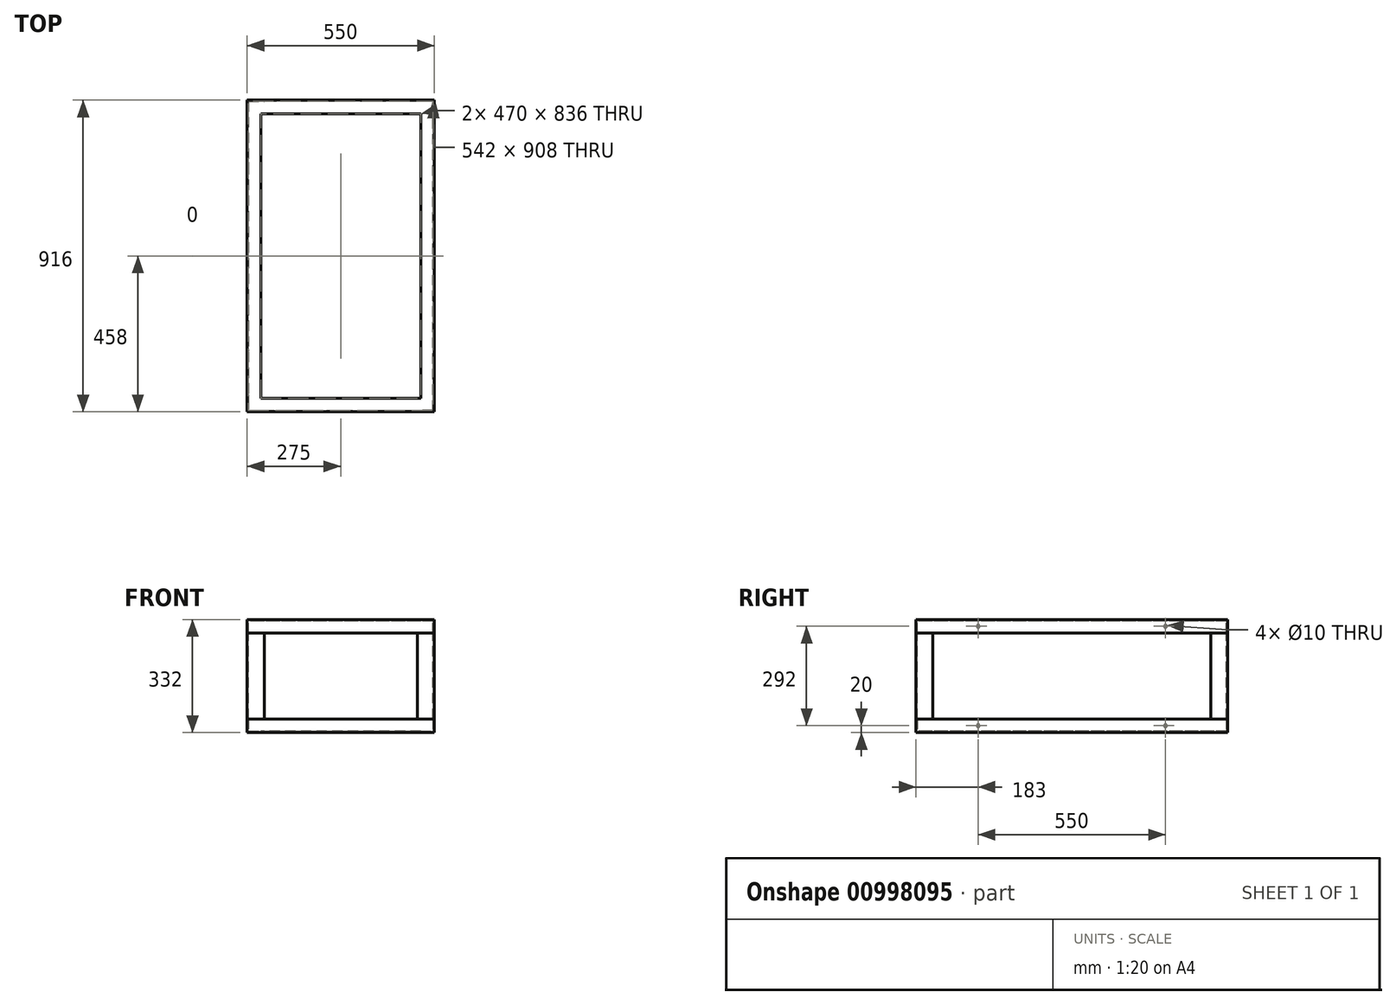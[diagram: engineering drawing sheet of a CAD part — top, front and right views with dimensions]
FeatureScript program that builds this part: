
annotation { "Feature Type Name" : "Feature", "Feature Type Description" : "" }
export const myFeature = defineFeature(function(context is Context, id is Id, definition is map)
    precondition{}
    {
        {
            var Q0;
            Q0=qCreatedBy(makeId("Top.planeOp"),FACE);
            var sketch = newSketch(context, id + "F0", { "sketchPlane" : qUnion([Q0])});
            skLineSegment(sketch, "E0.bottom", {"start": v(0, 0) * mm, "end": v(550, 0) * mm});
            skLineSegment(sketch, "E0.top", {"start": v(0, 916) * mm, "end": v(550, 916) * mm});
            skLineSegment(sketch, "E0.left", {"start": v(0, 0) * mm, "end": v(0, 916) * mm});
            skLineSegment(sketch, "E0.right", {"start": v(550, 0) * mm, "end": v(550, 916) * mm});
            skSolve(sketch);
        }
        {
            var Q0;
            Q0=qCreatedBy(makeId("Right.planeOp"),FACE);
            var sketch = newSketch(context, id + "F1", { "sketchPlane" : qUnion([Q0])});
            skLineSegment(sketch, "E1", {"start": v(0, 40) * mm, "end": v(0, 0) * mm});
            skLineSegment(sketch, "E2", {"start": v(0, 0) * mm, "end": v(40, 0) * mm});
            skLineSegment(sketch, "E3.0", {"start": v(4, 4) * mm, "end": v(40, 4) * mm});
            skLineSegment(sketch, "E3.1", {"start": v(4, 40) * mm, "end": v(4, 4) * mm});
            skLineSegment(sketch, "E4", {"start": v(40, 0) * mm, "end": v(40, 4) * mm});
            skLineSegment(sketch, "E5", {"start": v(0, 40) * mm, "end": v(4, 40) * mm});
            skSolve(sketch);
        }
        {
            var Q0;
            Q0=makeQuery(id+"F1.imprint","IMPRINT",FACE,{"disambiguationData":[TD([[makeQuery(id+"F1.imprint","IMPRINT",EDGE,{"derivedFrom":sQuery(id+"F1.wireOp",EDGE,"E1")}),1.0]])]});
            var Q1;
            Q1=sQuery(id+"F0.wireOp",EDGE,"E0.bottom");
            var Q2;
            Q2=sQuery(id+"F0.wireOp",EDGE,"E0.right");
            var Q3;
            Q3=sQuery(id+"F0.wireOp",EDGE,"E0.top");
            var Q4;
            Q4=sQuery(id+"F0.wireOp",EDGE,"E0.left");
            sweep(context, id + "F2", {"profiles" : qUnion([Q0]), "path" : qUnion([Q1, Q2, Q3, Q4])});
        }
        {
            var Q0;
            Q0=qCreatedBy(makeId("Top.planeOp"),FACE);
            cPlane(context, id + "F3", {"entities" : qUnion([Q0]), "cplaneType" : CPlaneType.OFFSET, "offset" : (332 / 2) * mm, "width" : 150 * mm, "height" : 150 * mm});
        }
        {
            var Q0;
            Q0=makeQuery(id+"F2.opSweep","SWEPT_BODY",BODY,{"disambiguationData":[OSD([sQuery(id+"F0.wireOp",EDGE,"E0.left"),sQuery(id+"F1.wireOp",EDGE,"E1"),sQuery(id+"F1.wireOp",EDGE,"E2"),sQuery(id+"F1.wireOp",EDGE,"E3.0"),sQuery(id+"F1.wireOp",EDGE,"E3.1"),sQuery(id+"F1.wireOp",EDGE,"E4"),sQuery(id+"F1.wireOp",EDGE,"E5")])]});
            var Q1;
            Q1=qCreatedBy(id+"F3.planeOp",FACE);
            mirror(context, id + "F4", {"entities" : qUnion([Q0]), "mirrorPlane" : qUnion([Q1])});
        }
        {
            var Q0;
            Q0=makeQuery(id+"F2.opSweep","SWEPT_FACE",FACE,{"disambiguationData":[OSD([sQuery(id+"F0.wireOp",EDGE,"E0.bottom"),sQuery(id+"F1.wireOp",EDGE,"E1")])]});
            var sketch = newSketch(context, id + "F5", { "sketchPlane" : qUnion([Q0])});
            skLineSegment(sketch, "E6", {"start": v(0, 40) * mm, "end": v(0, 292) * mm});
            skSolve(sketch);
        }
        {
            var Q0;
            Q0=makeQuery(id+"F2.opSweep","SWEPT_FACE",FACE,{"disambiguationData":[OSD([sQuery(id+"F0.wireOp",EDGE,"E0.bottom"),sQuery(id+"F1.wireOp",EDGE,"E5")])]});
            var sketch = newSketch(context, id + "F6", { "sketchPlane" : qUnion([Q0])});
            skLineSegment(sketch, "E7", {"start": v(0, 50) * mm, "end": v(0, 0) * mm});
            skLineSegment(sketch, "E8", {"start": v(0, 0) * mm, "end": v(50, 0) * mm});
            skLineSegment(sketch, "E9.0", {"start": v(5, 5) * mm, "end": v(50, 5) * mm});
            skLineSegment(sketch, "E9.1", {"start": v(5, 50) * mm, "end": v(5, 5) * mm});
            skLineSegment(sketch, "E10", {"start": v(0, 50) * mm, "end": v(5, 50) * mm});
            skLineSegment(sketch, "E11", {"start": v(50, 5) * mm, "end": v(50, 0) * mm});
            skSolve(sketch);
        }
        {
            var Q0;
            Q0=makeQuery(id+"F6.imprint","IMPRINT",FACE,{"disambiguationData":[TD([[makeQuery(id+"F6.imprint","IMPRINT",EDGE,{"derivedFrom":sQuery(id+"F6.wireOp",EDGE,"E7")}),1.0]])]});
            var Q1;
            Q1=sQuery(id+"F5.wireOp",EDGE,"E6");
            sweep(context, id + "F7", {"profiles" : qUnion([Q0]), "path" : qUnion([Q1])});
        }
        {
            var Q0;
            Q0=makeQuery(id+"F2.opSweep","SWEPT_EDGE",EDGE,{"disambiguationData":[OSD([sQuery(id+"F0.wireOp",EDGE,"E0.left"),sQuery(id+"F1.wireOp",EDGE,"E1"),sQuery(id+"F1.wireOp",EDGE,"E2")])]});
            cPoint(context, id + "F8", {"entities" : qUnion([Q0]), "parameter" : 0.5});
        }
        {
            var Q0;
            Q0 = qCreatedBy(id + "F8" ,VERTEX);
            var Q1;
            Q1=makeQuery(id+"F2.opSweep","SWEPT_EDGE",EDGE,{"disambiguationData":[OSD([sQuery(id+"F0.wireOp",EDGE,"E0.left"),sQuery(id+"F1.wireOp",EDGE,"E1"),sQuery(id+"F1.wireOp",EDGE,"E2")])]});
            cPlane(context, id + "F9", {"entities" : qUnion([Q0, Q1]), "cplaneType" : CPlaneType.LINE_POINT, "offset" : 531 * mm, "oppositeDirection" : true, "width" : 150 * mm, "height" : 150 * mm});
        }
        {
            var Q0;
            Q0=makeQuery(id+"F7.opSweep","SWEPT_BODY",BODY,{"disambiguationData":[OSD([sQuery(id+"F5.wireOp",EDGE,"E6"),sQuery(id+"F6.wireOp",EDGE,"E7"),sQuery(id+"F6.wireOp",EDGE,"E8"),sQuery(id+"F6.wireOp",EDGE,"E9.0"),sQuery(id+"F6.wireOp",EDGE,"E9.1"),sQuery(id+"F6.wireOp",EDGE,"E10"),sQuery(id+"F6.wireOp",EDGE,"E11")])]});
            var Q1;
            Q1=qCreatedBy(id+"F9.planeOp",FACE);
            mirror(context, id + "F10", {"entities" : qUnion([Q0]), "mirrorPlane" : qUnion([Q1])});
        }
        {
            var Q0;
            Q0=makeQuery(id+"F2.opSweep","SWEPT_EDGE",EDGE,{"disambiguationData":[OSD([sQuery(id+"F0.wireOp",EDGE,"E0.bottom"),sQuery(id+"F1.wireOp",EDGE,"E1"),sQuery(id+"F1.wireOp",EDGE,"E2")])]});
            cPoint(context, id + "F11", {"entities" : qUnion([Q0]), "parameter" : 0.5});
        }
        {
            var Q0;
            Q0=makeQuery(id+"F2.opSweep","SWEPT_EDGE",EDGE,{"disambiguationData":[OSD([sQuery(id+"F0.wireOp",EDGE,"E0.bottom"),sQuery(id+"F1.wireOp",EDGE,"E1"),sQuery(id+"F1.wireOp",EDGE,"E2")])]});
            var Q1;
            Q1 = qCreatedBy(id + "F11" ,VERTEX);
            cPlane(context, id + "F12", {"entities" : qUnion([Q0, Q1]), "cplaneType" : CPlaneType.LINE_POINT, "offset" : 256 * mm, "width" : 150 * mm, "height" : 150 * mm});
        }
        {
            var Q0;
            Q0=makeQuery(id+"F7.opSweep","SWEPT_BODY",BODY,{"disambiguationData":[OSD([sQuery(id+"F5.wireOp",EDGE,"E6"),sQuery(id+"F6.wireOp",EDGE,"E7"),sQuery(id+"F6.wireOp",EDGE,"E8"),sQuery(id+"F6.wireOp",EDGE,"E9.0"),sQuery(id+"F6.wireOp",EDGE,"E9.1"),sQuery(id+"F6.wireOp",EDGE,"E10"),sQuery(id+"F6.wireOp",EDGE,"E11")])]});
            var Q1;
            Q1=makeQuery(id+"F10.opPattern","COPY",BODY,{"derivedFrom":makeQuery(id+"F7.opSweep","SWEPT_BODY",BODY,{"disambiguationData":[OSD([sQuery(id+"F5.wireOp",EDGE,"E6"),sQuery(id+"F6.wireOp",EDGE,"E7"),sQuery(id+"F6.wireOp",EDGE,"E8"),sQuery(id+"F6.wireOp",EDGE,"E9.0"),sQuery(id+"F6.wireOp",EDGE,"E9.1"),sQuery(id+"F6.wireOp",EDGE,"E10"),sQuery(id+"F6.wireOp",EDGE,"E11")])]}),"instanceName":"1"});
            var Q2;
            Q2=qCreatedBy(id+"F12.planeOp",FACE);
            mirror(context, id + "F13", {"entities" : qUnion([Q0, Q1]), "mirrorPlane" : qUnion([Q2])});
        }
        {
            var Q0;
            Q0=makeQuery(id+"F4.opPattern","COPY",FACE,{"derivedFrom":makeQuery(id+"F2.opSweep","SWEPT_FACE",FACE,{"disambiguationData":[OSD([sQuery(id+"F0.wireOp",EDGE,"E0.left"),sQuery(id+"F1.wireOp",EDGE,"E1")])]}),"instanceName":"1"});
            var sketch = newSketch(context, id + "F14", { "sketchPlane" : qUnion([Q0])});
            skCircle(sketch, "E12", {"center": v(-733, 312) * mm, "radius": 5 * mm});
            skPoint(sketch, "E12.centerSnap0", {"position": v(-916, 312) * mm});
            skCircle(sketch, "E13", {"center": v(-183, 312) * mm, "radius": 5 * mm});
            skCircle(sketch, "E14.MirrorC", {"center": v(-183, 20) * mm, "radius": 5 * mm});
            skCircle(sketch, "E15.MirrorC", {"center": v(-733, 20) * mm, "radius": 5 * mm});
            skSolve(sketch);
        }
        {
            var Q0;
            Q0=qSketchRegion(id+"F14",true);
            var Q1;
            Q1=makeQuery(id+"F4.opPattern","COPY",FACE,{"derivedFrom":makeQuery(id+"F2.opSweep","SWEPT_FACE",FACE,{"disambiguationData":[OSD([sQuery(id+"F0.wireOp",EDGE,"E0.right"),sQuery(id+"F1.wireOp",EDGE,"E1")])]}),"instanceName":"1"});
            extrude(context, id + "F15", {"entities" : qUnion([Q0]), "operationType" : NewBodyOperationType.REMOVE, "endBound" : BoundingType.UP_TO_NEXT, "oppositeDirection" : true, "depth" : 25 * mm, "endBoundEntityFace" : qUnion([Q1]), "offsetDistance" : 25 * mm});
        }
    });
